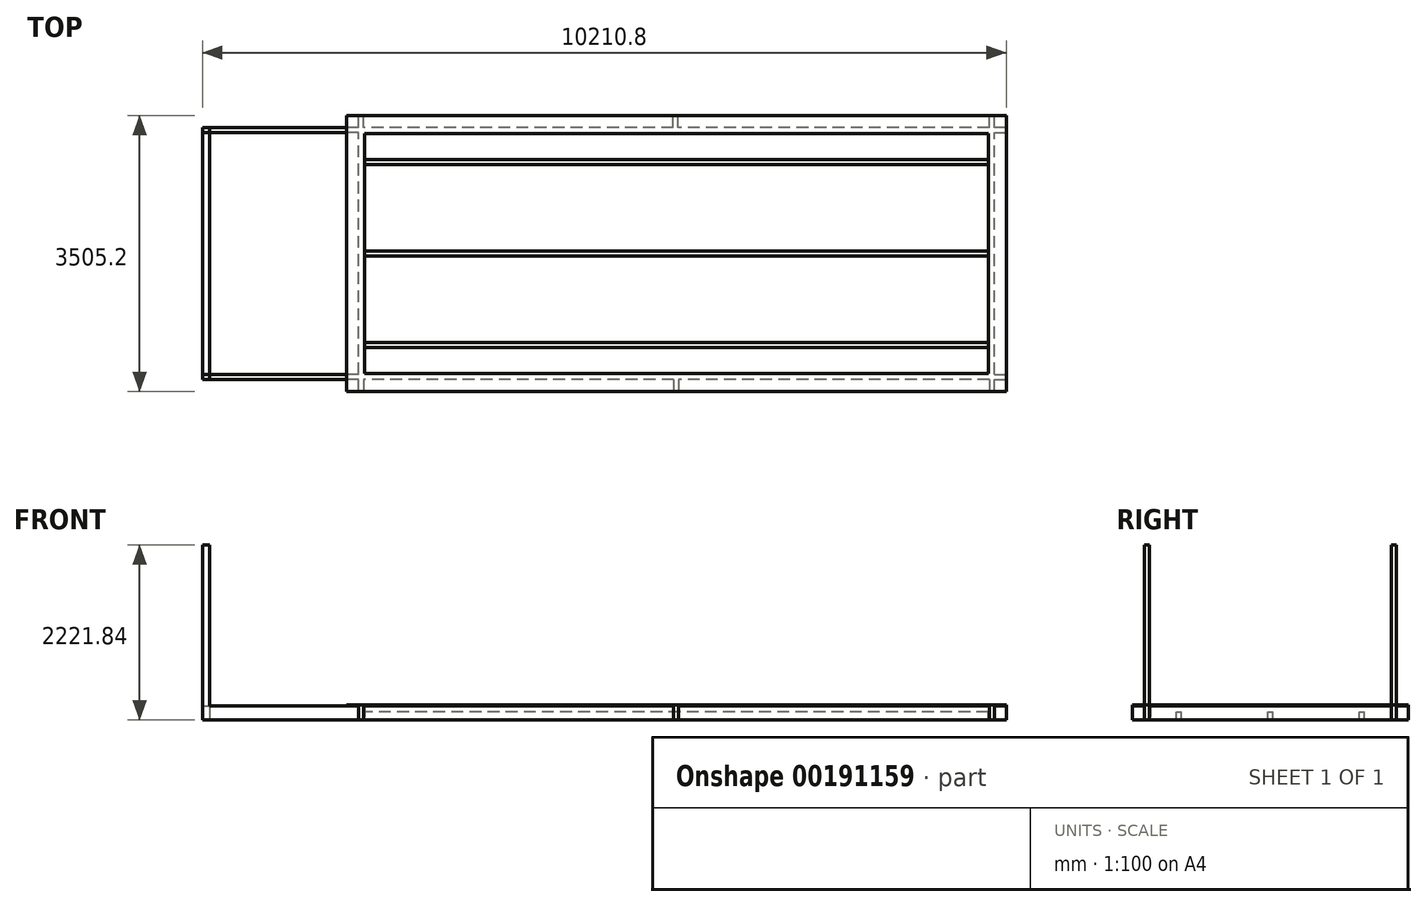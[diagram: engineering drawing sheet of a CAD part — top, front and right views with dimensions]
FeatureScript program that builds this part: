
annotation { "Feature Type Name" : "Feature", "Feature Type Description" : "" }
export const myFeature = defineFeature(function(context is Context, id is Id, definition is map)
    precondition{}
    {
        {
            var Q0;
            Q0=qCreatedBy(makeId("Top.planeOp"),FACE);
            var sketch = newSketch(context, id + "F0", { "sketchPlane" : qUnion([Q0])});
            skLineSegment(sketch, "E0.bottom", {"start": v(3962.4, -1524) * mm, "end": v(-3962.4, -1524) * mm});
            skLineSegment(sketch, "E0.top", {"start": v(3962.4, 1524) * mm, "end": v(-3962.4, 1524) * mm});
            skLineSegment(sketch, "E0.left", {"start": v(3962.4, -1524) * mm, "end": v(3962.4, 1524) * mm});
            skLineSegment(sketch, "E0.right", {"start": v(-3962.4, -1524) * mm, "end": v(-3962.4, 1524) * mm});
            skPoint(sketch, "E0.middle", {"position": v(0, 0) * mm});
            skLineSegment(sketch, "E1.bottom", {"start": v(4038.6, -1600.2) * mm, "end": v(-4038.6, -1600.2) * mm});
            skLineSegment(sketch, "E1.top", {"start": v(4038.6, 1600.2) * mm, "end": v(-4038.6, 1600.2) * mm});
            skLineSegment(sketch, "E1.left", {"start": v(4038.6, -1600.2) * mm, "end": v(4038.6, 1600.2) * mm});
            skLineSegment(sketch, "E1.right", {"start": v(-4038.6, -1600.2) * mm, "end": v(-4038.6, 1600.2) * mm});
            skSolve(sketch);
        }
        {
            var Q0;
            Q0 = qSketchRegion(id + "F0", true);
            extrude(context, id + "F1", {"entities" : qUnion([Q0]), "depth" : 88.9 * mm});
        }
        {
            var Q0;
            Q0=makeQuery(id+"F1.opExtrude","CAP_FACE",FACE,{"disambiguationData":[OSD([sQuery(id+"F0.wireOp",EDGE,"E0.bottom"),sQuery(id+"F0.wireOp",EDGE,"E0.top"),sQuery(id+"F0.wireOp",EDGE,"E0.left"),sQuery(id+"F0.wireOp",EDGE,"E0.right"),sQuery(id+"F0.wireOp",EDGE,"E1.bottom"),sQuery(id+"F0.wireOp",EDGE,"E1.top"),sQuery(id+"F0.wireOp",EDGE,"E1.left"),sQuery(id+"F0.wireOp",EDGE,"E1.right")])],"isStart":false});
            var sketch = newSketch(context, id + "F2", { "sketchPlane" : qUnion([Q0])});
            skLineSegment(sketch, "E2.bottom", {"start": v(4038.6, -1600.2) * mm, "end": v(-4038.6, -1600.2) * mm});
            skLineSegment(sketch, "E2.top", {"start": v(4038.6, 1600.2) * mm, "end": v(-4038.6, 1600.2) * mm});
            skLineSegment(sketch, "E2.left", {"start": v(4038.6, -1600.2) * mm, "end": v(4038.6, 1600.2) * mm});
            skLineSegment(sketch, "E2.right", {"start": v(-4038.6, -1600.2) * mm, "end": v(-4038.6, 1600.2) * mm});
            skPoint(sketch, "E2.middle", {"position": v(0, 0) * mm});
            skLineSegment(sketch, "E3.bottom", {"start": v(4191, -1752.6) * mm, "end": v(-4191, -1752.6) * mm});
            skLineSegment(sketch, "E3.top", {"start": v(4191, 1752.6) * mm, "end": v(-4191, 1752.6) * mm});
            skLineSegment(sketch, "E3.left", {"start": v(4191, -1752.6) * mm, "end": v(4191, 1752.6) * mm});
            skLineSegment(sketch, "E3.right", {"start": v(-4191, -1752.6) * mm, "end": v(-4191, 1752.6) * mm});
            skSolve(sketch);
        }
        {
            var Q0;
            Q0 = qSketchRegion(id + "F2", true);
            extrude(context, id + "F3", {"entities" : qUnion([Q0]), "operationType" : NewBodyOperationType.ADD, "oppositeDirection" : true, "depth" : 12.7 * mm});
        }
        {
            var Q0;
            Q0=makeQuery(id+"F1.opExtrude","CAP_FACE",FACE,{"disambiguationData":[OSD([sQuery(id+"F0.wireOp",EDGE,"E0.bottom"),sQuery(id+"F0.wireOp",EDGE,"E0.top"),sQuery(id+"F0.wireOp",EDGE,"E0.left"),sQuery(id+"F0.wireOp",EDGE,"E0.right"),sQuery(id+"F0.wireOp",EDGE,"E1.bottom"),sQuery(id+"F0.wireOp",EDGE,"E1.top"),sQuery(id+"F0.wireOp",EDGE,"E1.left"),sQuery(id+"F0.wireOp",EDGE,"E1.right")])],"isStart":true});
            var sketch = newSketch(context, id + "F4", { "sketchPlane" : qUnion([Q0])});
            skLineSegment(sketch, "E4.bottom", {"start": v(-4038.6, -1193.8) * mm, "end": v(4038.6, -1193.8) * mm});
            skLineSegment(sketch, "E4.top", {"start": v(-4038.6, -1130.3) * mm, "end": v(4038.6, -1130.3) * mm});
            skLineSegment(sketch, "E4.left", {"start": v(-4038.6, -1193.8) * mm, "end": v(-4038.6, -1130.3) * mm});
            skLineSegment(sketch, "E4.right", {"start": v(4038.6, -1193.8) * mm, "end": v(4038.6, -1130.3) * mm});
            skLineSegment(sketch, "E5.bottom", {"start": v(-4038.6, 31.75) * mm, "end": v(4038.6, 31.75) * mm});
            skLineSegment(sketch, "E5.top", {"start": v(-4038.6, -31.75) * mm, "end": v(4038.6, -31.75) * mm});
            skLineSegment(sketch, "E5.left", {"start": v(-4038.6, 31.75) * mm, "end": v(-4038.6, -31.75) * mm});
            skLineSegment(sketch, "E5.right", {"start": v(4038.6, 31.75) * mm, "end": v(4038.6, -31.75) * mm});
            skPoint(sketch, "E5.middle", {"position": v(0, 0) * mm});
            skLineSegment(sketch, "E6.bottom", {"start": v(4038.6, 1130.3) * mm, "end": v(-4038.6, 1130.3) * mm});
            skLineSegment(sketch, "E6.top", {"start": v(4038.6, 1193.8) * mm, "end": v(-4038.6, 1193.8) * mm});
            skLineSegment(sketch, "E6.left", {"start": v(4038.6, 1130.3) * mm, "end": v(4038.6, 1193.8) * mm});
            skLineSegment(sketch, "E6.right", {"start": v(-4038.6, 1130.3) * mm, "end": v(-4038.6, 1193.8) * mm});
            skLineSegment(sketch, "E7.bottom", {"start": v(-4038.6, -1600.2) * mm, "end": v(-3962.4, -1600.2) * mm});
            skLineSegment(sketch, "E7.top", {"start": v(-4038.6, 1600.2) * mm, "end": v(-3962.4, 1600.2) * mm});
            skLineSegment(sketch, "E7.left", {"start": v(-4038.6, -1600.2) * mm, "end": v(-4038.6, 1600.2) * mm});
            skLineSegment(sketch, "E7.right", {"start": v(-3962.4, -1600.2) * mm, "end": v(-3962.4, 1600.2) * mm});
            skLineSegment(sketch, "E8.bottom", {"start": v(4038.6, -1600.2) * mm, "end": v(3962.4, -1600.2) * mm});
            skLineSegment(sketch, "E8.top", {"start": v(4038.6, 1600.2) * mm, "end": v(3962.4, 1600.2) * mm});
            skLineSegment(sketch, "E8.left", {"start": v(4038.6, -1600.2) * mm, "end": v(4038.6, 1600.2) * mm});
            skLineSegment(sketch, "E8.right", {"start": v(3962.4, -1600.2) * mm, "end": v(3962.4, 1600.2) * mm});
            skSolve(sketch);
        }
        {
            var Q0;
            Q0 = qSketchRegion(id + "F4", true);
            var Q1;
            {var subQ0=sQuery(id+"F4.wireOp",EDGE,"E7.right");var subQ1=sQuery(id+"F4.wireOp",EDGE,"E5.bottom");var subQ2=makeQuery(id+"F4.imprint","INTERSECT",VERTEX,{"derivedFrom":[subQ1,subQ0]});Q1=makeQuery(id+"F4.imprint","IMPRINT",FACE,{"disambiguationData":[TD([[makeQuery(id+"F4.imprint","IMPRINT",EDGE,{"disambiguationData":[TD([[subQ2,-1.0]])],"derivedFrom":subQ1}),-1.0]])]});}
            extrude(context, id + "F5", {"entities" : qUnion([Q0, Q1]), "operationType" : NewBodyOperationType.ADD, "depth" : 101.6 * mm});
        }
        {
            var Q0;
            {var subQ1=sQuery(id+"F0.wireOp",EDGE,"E0.top");var subQ6=sQuery(id+"F0.wireOp",EDGE,"E1.top");var subQ11=sQuery(id+"F0.wireOp",EDGE,"E0.bottom");var subQ14=sQuery(id+"F0.wireOp",EDGE,"E1.bottom");var subQ17=sQuery(id+"F0.wireOp",EDGE,"E0.right");var subQ22=sQuery(id+"F0.wireOp",EDGE,"E0.left");Q0=makeQuery(id+"F5.boolean.opBoolean","SPLIT",FACE,{"disambiguationData":[TD([makeQuery(id+"F1.opExtrude","SWEPT_FACE",FACE,{"disambiguationData":[OSD([subQ1])]})])],"derivedFrom":makeQuery(id+"F1.opExtrude","CAP_FACE",FACE,{"disambiguationData":[OSD([subQ11,subQ1,subQ22,subQ17,subQ14,subQ6,sQuery(id+"F0.wireOp",EDGE,"E1.left"),sQuery(id+"F0.wireOp",EDGE,"E1.right")])],"isStart":true})});}
            var sketch = newSketch(context, id + "F6", { "sketchPlane" : qUnion([Q0])});
            skLineSegment(sketch, "E9.bottom", {"start": v(-3962.4, -1600.2) * mm, "end": v(3962.4, -1600.2) * mm});
            skLineSegment(sketch, "E9.top", {"start": v(-3962.4, -1524) * mm, "end": v(3962.4, -1524) * mm});
            skLineSegment(sketch, "E9.left", {"start": v(-3962.4, -1600.2) * mm, "end": v(-3962.4, -1524) * mm});
            skLineSegment(sketch, "E9.right", {"start": v(3962.4, -1600.2) * mm, "end": v(3962.4, -1524) * mm});
            skSolve(sketch);
        }
        {
            var Q0;
            Q0 = qSketchRegion(id + "F6", true);
            extrude(context, id + "F7", {"entities" : qUnion([Q0]), "operationType" : NewBodyOperationType.ADD, "depth" : 101.6 * mm});
        }
        {
            var Q0;
            {var subQ1=sQuery(id+"F0.wireOp",EDGE,"E0.bottom");var subQ8=sQuery(id+"F0.wireOp",EDGE,"E1.bottom");var subQ11=sQuery(id+"F0.wireOp",EDGE,"E0.right");var subQ13=sQuery(id+"F0.wireOp",EDGE,"E0.top");var subQ17=sQuery(id+"F0.wireOp",EDGE,"E1.top");var subQ19=sQuery(id+"F0.wireOp",EDGE,"E0.left");Q0=makeQuery(id+"F5.boolean.opBoolean","SPLIT",FACE,{"disambiguationData":[TD([makeQuery(id+"F1.opExtrude","SWEPT_FACE",FACE,{"disambiguationData":[OSD([subQ1])]})])],"derivedFrom":makeQuery(id+"F1.opExtrude","CAP_FACE",FACE,{"disambiguationData":[OSD([subQ1,subQ13,subQ19,subQ11,subQ8,subQ17,sQuery(id+"F0.wireOp",EDGE,"E1.left"),sQuery(id+"F0.wireOp",EDGE,"E1.right")])],"isStart":true})});}
            var sketch = newSketch(context, id + "F8", { "sketchPlane" : qUnion([Q0])});
            skLineSegment(sketch, "E10.bottom", {"start": v(3962.4, 1600.2) * mm, "end": v(-3962.4, 1600.2) * mm});
            skLineSegment(sketch, "E10.top", {"start": v(3962.4, 1524) * mm, "end": v(-3962.4, 1524) * mm});
            skLineSegment(sketch, "E10.left", {"start": v(3962.4, 1600.2) * mm, "end": v(3962.4, 1524) * mm});
            skLineSegment(sketch, "E10.right", {"start": v(-3962.4, 1600.2) * mm, "end": v(-3962.4, 1524) * mm});
            skSolve(sketch);
        }
        {
            var Q0;
            Q0 = qSketchRegion(id + "F8", true);
            extrude(context, id + "F9", {"entities" : qUnion([Q0]), "operationType" : NewBodyOperationType.ADD, "depth" : 101.6 * mm});
        }
        {
            var Q0;
            Q0=makeQuery(id+"F3.opExtrude","CAP_FACE",FACE,{"disambiguationData":[OSD([sQuery(id+"F2.wireOp",EDGE,"E2.bottom"),sQuery(id+"F2.wireOp",EDGE,"E2.top"),sQuery(id+"F2.wireOp",EDGE,"E2.left"),sQuery(id+"F2.wireOp",EDGE,"E2.right"),sQuery(id+"F2.wireOp",EDGE,"E3.bottom"),sQuery(id+"F2.wireOp",EDGE,"E3.top"),sQuery(id+"F2.wireOp",EDGE,"E3.left"),sQuery(id+"F2.wireOp",EDGE,"E3.right")])],"isStart":false});
            var sketch = newSketch(context, id + "F10", { "sketchPlane" : qUnion([Q0])});
            skLineSegment(sketch, "E11.bottom", {"start": v(-4038.6, 1600.2) * mm, "end": v(-3975.1, 1600.2) * mm});
            skLineSegment(sketch, "E11.top", {"start": v(-4038.6, 1752.6) * mm, "end": v(-3975.1, 1752.6) * mm});
            skLineSegment(sketch, "E11.left", {"start": v(-4038.6, 1600.2) * mm, "end": v(-4038.6, 1752.6) * mm});
            skLineSegment(sketch, "E11.right", {"start": v(-3975.1, 1600.2) * mm, "end": v(-3975.1, 1752.6) * mm});
            skLineSegment(sketch, "E12.bottom", {"start": v(-34.69, 1600.2) * mm, "end": v(28.81, 1600.2) * mm});
            skLineSegment(sketch, "E12.top", {"start": v(-34.69, 1752.6) * mm, "end": v(28.81, 1752.6) * mm});
            skLineSegment(sketch, "E12.left", {"start": v(-34.69, 1600.2) * mm, "end": v(-34.69, 1752.6) * mm});
            skLineSegment(sketch, "E12.right", {"start": v(28.81, 1600.2) * mm, "end": v(28.81, 1752.6) * mm});
            skLineSegment(sketch, "E13.bottom", {"start": v(4038.6, 1600.2) * mm, "end": v(3975.1, 1600.2) * mm});
            skLineSegment(sketch, "E13.top", {"start": v(4038.6, 1752.6) * mm, "end": v(3975.1, 1752.6) * mm});
            skLineSegment(sketch, "E13.left", {"start": v(4038.6, 1600.2) * mm, "end": v(4038.6, 1752.6) * mm});
            skLineSegment(sketch, "E13.right", {"start": v(3975.1, 1600.2) * mm, "end": v(3975.1, 1752.6) * mm});
            skLineSegment(sketch, "E14.bottom", {"start": v(4038.6, 1600.2) * mm, "end": v(4191, 1600.2) * mm});
            skLineSegment(sketch, "E14.top", {"start": v(4038.6, 1536.7) * mm, "end": v(4191, 1536.7) * mm});
            skLineSegment(sketch, "E14.left", {"start": v(4038.6, 1600.2) * mm, "end": v(4038.6, 1536.7) * mm});
            skLineSegment(sketch, "E14.right", {"start": v(4191, 1600.2) * mm, "end": v(4191, 1536.7) * mm});
            skLineSegment(sketch, "E15.bottom", {"start": v(4038.6, -1600.2) * mm, "end": v(4191, -1600.2) * mm});
            skLineSegment(sketch, "E15.top", {"start": v(4038.6, -1536.7) * mm, "end": v(4191, -1536.7) * mm});
            skLineSegment(sketch, "E15.left", {"start": v(4038.6, -1600.2) * mm, "end": v(4038.6, -1536.7) * mm});
            skLineSegment(sketch, "E15.right", {"start": v(4191, -1600.2) * mm, "end": v(4191, -1536.7) * mm});
            skLineSegment(sketch, "E16.bottom", {"start": v(4038.6, -1600.2) * mm, "end": v(3975.1, -1600.2) * mm});
            skLineSegment(sketch, "E16.top", {"start": v(4038.6, -1752.6) * mm, "end": v(3975.1, -1752.6) * mm});
            skLineSegment(sketch, "E16.left", {"start": v(4038.6, -1600.2) * mm, "end": v(4038.6, -1752.6) * mm});
            skLineSegment(sketch, "E16.right", {"start": v(3975.1, -1600.2) * mm, "end": v(3975.1, -1752.6) * mm});
            skLineSegment(sketch, "E17.bottom", {"start": v(-4038.6, -1600.2) * mm, "end": v(-3975.1, -1600.2) * mm});
            skLineSegment(sketch, "E17.top", {"start": v(-4038.6, -1752.6) * mm, "end": v(-3975.1, -1752.6) * mm});
            skLineSegment(sketch, "E17.left", {"start": v(-4038.6, -1600.2) * mm, "end": v(-4038.6, -1752.6) * mm});
            skLineSegment(sketch, "E17.right", {"start": v(-3975.1, -1600.2) * mm, "end": v(-3975.1, -1752.6) * mm});
            skLineSegment(sketch, "E18.bottom", {"start": v(-4038.6, -1600.2) * mm, "end": v(-4191, -1600.2) * mm});
            skLineSegment(sketch, "E18.top", {"start": v(-4038.6, -1536.7) * mm, "end": v(-4191, -1536.7) * mm});
            skLineSegment(sketch, "E18.left", {"start": v(-4038.6, -1600.2) * mm, "end": v(-4038.6, -1536.7) * mm});
            skLineSegment(sketch, "E18.right", {"start": v(-4191, -1600.2) * mm, "end": v(-4191, -1536.7) * mm});
            skLineSegment(sketch, "E19.bottom", {"start": v(-41.58, -1600.2) * mm, "end": v(21.92, -1600.2) * mm});
            skLineSegment(sketch, "E19.top", {"start": v(-41.58, -1752.6) * mm, "end": v(21.92, -1752.6) * mm});
            skLineSegment(sketch, "E19.left", {"start": v(-41.58, -1600.2) * mm, "end": v(-41.58, -1752.6) * mm});
            skLineSegment(sketch, "E19.right", {"start": v(21.92, -1600.2) * mm, "end": v(21.92, -1752.6) * mm});
            skLineSegment(sketch, "E20.bottom", {"start": v(-4038.6, 1600.2) * mm, "end": v(-4191, 1600.2) * mm});
            skLineSegment(sketch, "E20.top", {"start": v(-4038.6, 1536.7) * mm, "end": v(-4191, 1536.7) * mm});
            skLineSegment(sketch, "E20.left", {"start": v(-4038.6, 1600.2) * mm, "end": v(-4038.6, 1536.7) * mm});
            skLineSegment(sketch, "E20.right", {"start": v(-4191, 1600.2) * mm, "end": v(-4191, 1536.7) * mm});
            skSolve(sketch);
        }
        {
            var Q0;
            Q0 = qSketchRegion(id + "F10", true);
            extrude(context, id + "F11", {"entities" : qUnion([Q0]), "operationType" : NewBodyOperationType.ADD, "depth" : 177.8 * mm});
        }
        {
            var Q0;
            Q0=makeQuery(id+"F11.boolean.opBoolean","MERGE",FACE,{"derivedFrom":[makeQuery(id+"F3.opExtrude","SWEPT_FACE",FACE,{"disambiguationData":[OSD([sQuery(id+"F2.wireOp",EDGE,"E3.right")])]}),makeQuery(id+"F11.opExtrude","SWEPT_FACE",FACE,{"disambiguationData":[OSD([sQuery(id+"F10.wireOp",EDGE,"E18.right")])]}),makeQuery(id+"F11.opExtrude","SWEPT_FACE",FACE,{"disambiguationData":[OSD([sQuery(id+"F10.wireOp",EDGE,"E20.right")])]})]});
            var sketch = newSketch(context, id + "F12", { "sketchPlane" : qUnion([Q0])});
            skLineSegment(sketch, "E21", {"start": v(1536.7, 76.2) * mm, "end": v(1600.2, 76.2) * mm});
            skLineSegment(sketch, "E22", {"start": v(-1600.2, 76.2) * mm, "end": v(-1536.7, 76.2) * mm});
            skSolve(sketch);
        }
        {
            var Q0;
            Q0=makeQuery(id+"F12.imprint","IMPRINT",FACE,{"disambiguationData":[TD([[makeQuery(id+"F12.imprint","IMPRINT",EDGE,{"derivedFrom":sQuery(id+"F12.wireOp",EDGE,"E22")}),-1.0]])]});
            var Q1;
            Q1=makeQuery(id+"F12.imprint","IMPRINT",FACE,{"disambiguationData":[TD([[makeQuery(id+"F12.imprint","IMPRINT",EDGE,{"derivedFrom":sQuery(id+"F12.wireOp",EDGE,"E21")}),-1.0]])]});
            extrude(context, id + "F13", {"entities" : qUnion([Q0, Q1]), "operationType" : NewBodyOperationType.ADD, "depth" : 1828.8 * mm, "offsetDistance" : 25.4 * mm});
        }
        {
            var Q0;
            {var subQ0=sQuery(id+"F10.wireOp",EDGE,"E18.top");Q0=makeQuery(id+"F13.boolean.opBoolean","MERGE",FACE,{"derivedFrom":[makeQuery(id+"F11.opExtrude","SWEPT_FACE",FACE,{"disambiguationData":[OSD([subQ0])]}),makeQuery(id+"F13.opExtrude","SWEPT_FACE",FACE,{"disambiguationData":[OSD([sQuery(id+"F2.wireOp",EDGE,"E3.right"),subQ0,sQuery(id+"F10.wireOp",EDGE,"E18.right")])]})]});}
            var sketch = newSketch(context, id + "F14", { "sketchPlane" : qUnion([Q0])});
            skLineSegment(sketch, "E23", {"start": v(-5930.9, 76.2) * mm, "end": v(-5930.9, -101.6) * mm});
            skSolve(sketch);
        }
        {
            var Q0;
            Q0 = qSketchRegion(id + "F14", true);
            var Q1;
            {var subQ0=sQuery(id+"F14.wireOp",EDGE,"E23");Q1=makeQuery(id+"F14.imprint","IMPRINT",FACE,{"disambiguationData":[TD([[makeQuery(id+"F14.imprint","IMPRINT",EDGE,{"derivedFrom":subQ0}),-1.0]])]});}
            extrude(context, id + "F15", {"entities" : qUnion([Q0, Q1]), "operationType" : NewBodyOperationType.ADD, "depth" : 3103.88 * mm, "offsetDistance" : 25.4 * mm});
        }
        {
            var Q0;
            {var subQ0=sQuery(id+"F12.wireOp",EDGE,"E22");Q0=makeQuery(id+"F15.boolean.opBoolean","MERGE",FACE,{"derivedFrom":[makeQuery(id+"F13.opExtrude","SWEPT_FACE",FACE,{"disambiguationData":[OSD([sQuery(id+"F12.wireOp",EDGE,"E21")])]}),makeQuery(id+"F13.opExtrude","SWEPT_FACE",FACE,{"disambiguationData":[OSD([subQ0])]}),makeQuery(id+"F15.opExtrude","SWEPT_FACE",FACE,{"disambiguationData":[OSD([sQuery(id+"F2.wireOp",EDGE,"E3.right"),sQuery(id+"F10.wireOp",EDGE,"E18.top"),sQuery(id+"F10.wireOp",EDGE,"E18.right"),subQ0])]})]});}
            var sketch = newSketch(context, id + "F16", { "sketchPlane" : qUnion([Q0])});
            skLineSegment(sketch, "E24.bottom", {"start": v(-5930.9, -1536.7) * mm, "end": v(-6019.8, -1536.7) * mm});
            skLineSegment(sketch, "E24.top", {"start": v(-5930.9, -1600.2) * mm, "end": v(-6019.8, -1600.2) * mm});
            skLineSegment(sketch, "E24.left", {"start": v(-5930.9, -1536.7) * mm, "end": v(-5930.9, -1600.2) * mm});
            skLineSegment(sketch, "E24.right", {"start": v(-6019.8, -1536.7) * mm, "end": v(-6019.8, -1600.2) * mm});
            skLineSegment(sketch, "E25.bottom", {"start": v(-6019.8, 1600.2) * mm, "end": v(-5930.9, 1600.2) * mm});
            skLineSegment(sketch, "E25.top", {"start": v(-6019.8, 1536.7) * mm, "end": v(-5930.9, 1536.7) * mm});
            skLineSegment(sketch, "E25.left", {"start": v(-6019.8, 1600.2) * mm, "end": v(-6019.8, 1536.7) * mm});
            skLineSegment(sketch, "E25.right", {"start": v(-5930.9, 1600.2) * mm, "end": v(-5930.9, 1536.7) * mm});
            skSolve(sketch);
        }
        {
            var Q0;
            Q0 = qSketchRegion(id + "F16", true);
            extrude(context, id + "F17", {"entities" : qUnion([Q0]), "operationType" : NewBodyOperationType.ADD, "depth" : 2044.04 * mm, "offsetDistance" : 25.4 * mm});
        }
    });
